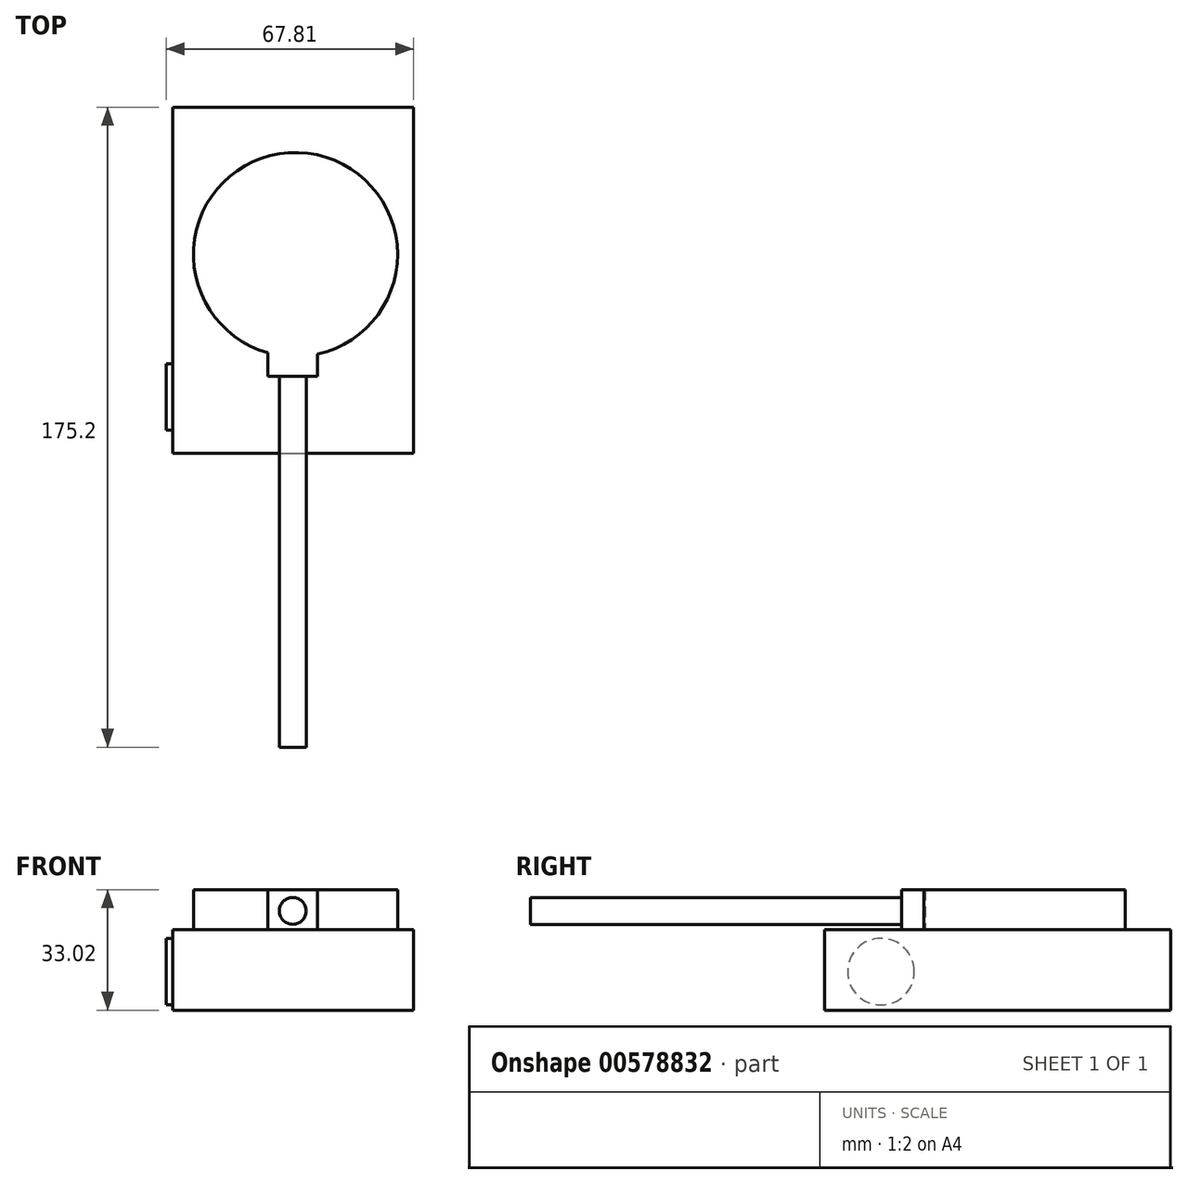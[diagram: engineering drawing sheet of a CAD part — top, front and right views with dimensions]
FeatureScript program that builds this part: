
annotation { "Feature Type Name" : "Feature", "Feature Type Description" : "" }
export const myFeature = defineFeature(function(context is Context, id is Id, definition is map)
    precondition{}
    {
        {
            var Q0;
            Q0=qCreatedBy(makeId("Top.planeOp"),FACE);
            var sketch = newSketch(context, id + "F0", { "sketchPlane" : qUnion([Q0])});
            skLineSegment(sketch, "E0.bottom", {"start": v(-33.66, 40.32) * mm, "end": v(32.37, 40.32) * mm});
            skLineSegment(sketch, "E0.top", {"start": v(-33.66, -54.42) * mm, "end": v(32.37, -54.42) * mm});
            skLineSegment(sketch, "E0.left", {"start": v(-33.66, 40.32) * mm, "end": v(-33.66, -54.42) * mm});
            skLineSegment(sketch, "E0.right", {"start": v(32.37, 40.32) * mm, "end": v(32.37, -54.42) * mm});
            skSolve(sketch);
        }
        {
            var Q0;
            Q0=makeQuery(id+"F0.imprint","IMPRINT",FACE,{"disambiguationData":[TD([[makeQuery(id+"F0.imprint","IMPRINT",EDGE,{"derivedFrom":sQuery(id+"F0.wireOp",EDGE,"E0.bottom")}),-1.0]])]});
            extrude(context, id + "F1", {"entities" : qUnion([Q0]), "depth" : 22.1 * mm, "offsetDistance" : 25.4 * mm});
        }
        {
            var Q0;
            Q0=makeQuery(id+"F1.opExtrude","CAP_FACE",FACE,{"disambiguationData":[OSD([sQuery(id+"F0.wireOp",EDGE,"E0.bottom"),sQuery(id+"F0.wireOp",EDGE,"E0.top"),sQuery(id+"F0.wireOp",EDGE,"E0.left"),sQuery(id+"F0.wireOp",EDGE,"E0.right")])],"isStart":false});
            var sketch = newSketch(context, id + "F2", { "sketchPlane" : qUnion([Q0])});
            skCircle(sketch, "E1", {"center": v(0, 0) * mm, "radius": 27.93 * mm});
            skLineSegment(sketch, "E2", {"start": v(-7.56, -26.9) * mm, "end": v(-7.56, -33.28) * mm});
            skLineSegment(sketch, "E3", {"start": v(-7.56, -33.28) * mm, "end": v(6.08, -33.28) * mm});
            skLineSegment(sketch, "E4", {"start": v(6.08, -33.28) * mm, "end": v(6.08, -27.26) * mm});
            skSolve(sketch);
        }
        {
            var Q0;
            Q0 = qSketchRegion(id + "F2", true);
            extrude(context, id + "F3", {"entities" : qUnion([Q0]), "depth" : 10.92 * mm, "offsetDistance" : 25.4 * mm});
        }
        {
            var Q0;
            Q0=makeQuery(id+"F3.opExtrude","SWEPT_FACE",FACE,{"disambiguationData":[OSD([sQuery(id+"F2.wireOp",EDGE,"E3")])]});
            var sketch = newSketch(context, id + "F4", { "sketchPlane" : qUnion([Q0])});
            skCircle(sketch, "E5", {"center": v(-0.74, 27.17) * mm, "radius": 3.66 * mm});
            skPoint(sketch, "E5.centerSnap0", {"position": v(-0.74, 22.1) * mm});
            skSolve(sketch);
        }
        {
            var Q0;
            Q0 = qSketchRegion(id + "F4", true);
            extrude(context, id + "F5", {"entities" : qUnion([Q0]), "operationType" : NewBodyOperationType.ADD, "depth" : 101.6 * mm, "offsetDistance" : 25.4 * mm});
        }
        {
            var Q0;
            Q0=makeQuery(id+"F1.opExtrude","SWEPT_FACE",FACE,{"disambiguationData":[OSD([sQuery(id+"F0.wireOp",EDGE,"E0.left")])]});
            var sketch = newSketch(context, id + "F6", { "sketchPlane" : qUnion([Q0])});
            skCircle(sketch, "E6", {"center": v(38.99, 10.54) * mm, "radius": 9.11 * mm});
            skSolve(sketch);
        }
        {
            var Q0;
            Q0=makeQuery(id+"F6.imprint","IMPRINT",FACE,{"disambiguationData":[TD([[makeQuery(id+"F6.imprint","IMPRINT",EDGE,{"derivedFrom":sQuery(id+"F6.wireOp",EDGE,"E6")}),1.0]])]});
            extrude(context, id + "F7", {"entities" : qUnion([Q0]), "depth" : 1.78 * mm, "offsetDistance" : 25.4 * mm});
        }
    });
